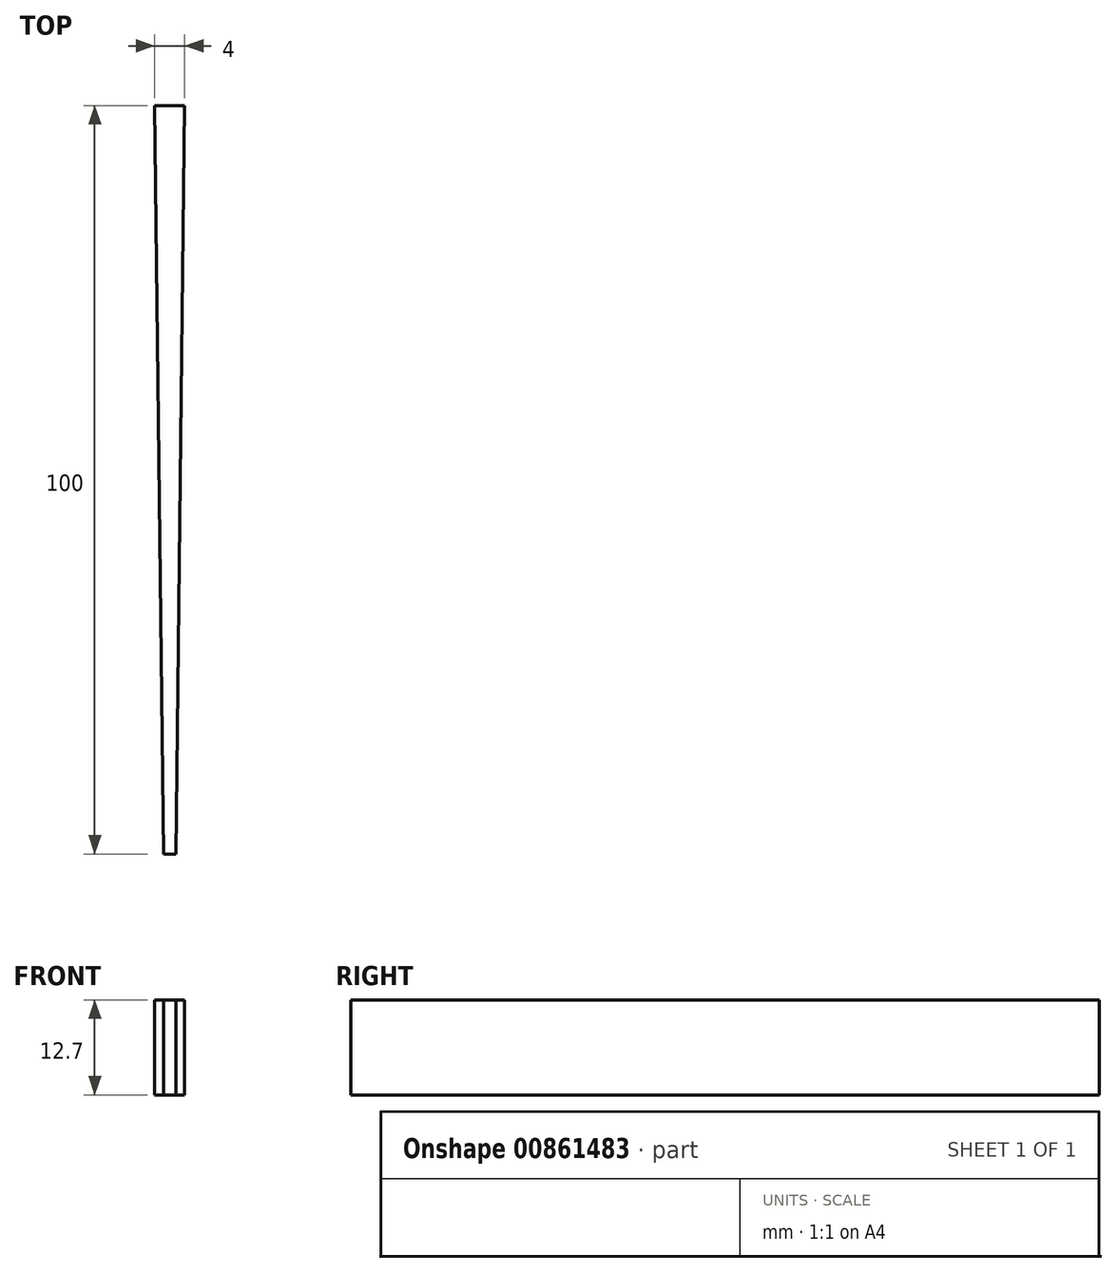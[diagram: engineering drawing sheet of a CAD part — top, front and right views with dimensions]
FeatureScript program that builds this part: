
annotation { "Feature Type Name" : "Feature", "Feature Type Description" : "" }
export const myFeature = defineFeature(function(context is Context, id is Id, definition is map)
    precondition{}
    {
        {
            var Q0;
            Q0=qCreatedBy(makeId("Top.planeOp"),FACE);
            var sketch = newSketch(context, id + "F0", { "sketchPlane" : qUnion([Q0])});
            skLineSegment(sketch, "E0", {"start": v(0.8, -100) * mm, "end": v(2, 0) * mm});
            skLineSegment(sketch, "E1", {"start": v(2, 0) * mm, "end": v(0, 0) * mm});
            skLineSegment(sketch, "E2", {"start": v(0, 0) * mm, "end": v(0, -100) * mm});
            skLineSegment(sketch, "E3", {"start": v(0, -100) * mm, "end": v(0.8, -100) * mm});
            skLineSegment(sketch, "E4.MirrorCS", {"start": v(-2, 0) * mm, "end": v(0, 0) * mm});
            skLineSegment(sketch, "E5.MirrorCS", {"start": v(0, -100) * mm, "end": v(-0.8, -100) * mm});
            skLineSegment(sketch, "E6.MirrorCS", {"start": v(-0.8, -100) * mm, "end": v(-2, 0) * mm});
            skSolve(sketch);
        }
        {
            var Q0;
            Q0=makeQuery(id+"F0.imprint","IMPRINT",FACE,{"disambiguationData":[TD([[makeQuery(id+"F0.imprint","IMPRINT",EDGE,{"derivedFrom":sQuery(id+"F0.wireOp",EDGE,"E2")}),-1.0]])]});
            var Q1;
            Q1=makeQuery(id+"F0.imprint","IMPRINT",FACE,{"disambiguationData":[TD([[makeQuery(id+"F0.imprint","IMPRINT",EDGE,{"derivedFrom":sQuery(id+"F0.wireOp",EDGE,"E0")}),1.0]])]});
            extrude(context, id + "F1", {"entities" : qUnion([Q0, Q1]), "depth" : 12.7 * mm, "offsetDistance" : 25.4 * mm});
        }
    });
